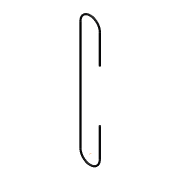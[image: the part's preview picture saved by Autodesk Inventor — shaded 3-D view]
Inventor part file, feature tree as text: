
AUTODESK INVENTOR PART (.ipt)
format: ipt  version: unknown  size: 193,536 bytes
history: native  units: in
note: dims shown in document units (in); Inventor stores cm internally (conversion verified against a paired STEP export)
features: sketch x3, projected_geometry x2, sweep x1, other x1, mirror x1, extrude x1
ambient origin geometry x8: Origin, YZ Plane, XZ Plane, XY Plane, X Axis, Y Axis, Z Axis, Center Point
feature tree (9):
  sweep  "Sweep5"
  other  "Work Axis9"
  mirror  "Mirror4"
  extrude  "Extrusion9"  Depth=0.2362in
  sketch  "Sketch10"  dims[d24=0.0in d33=1.3386in]
  sketch  "Sketch15"  dims[d35=0.0in d45=0.2362in]
  sketch  "Sketch20"  dims[d46=0.0394in d47=0.0in d56=0.2362in d57=0.0in d59=0.3937in d60=0.0in d61=0.7087in]
  projected_geometry  "Projected Loop1"
  projected_geometry  "Projected Loop2"
